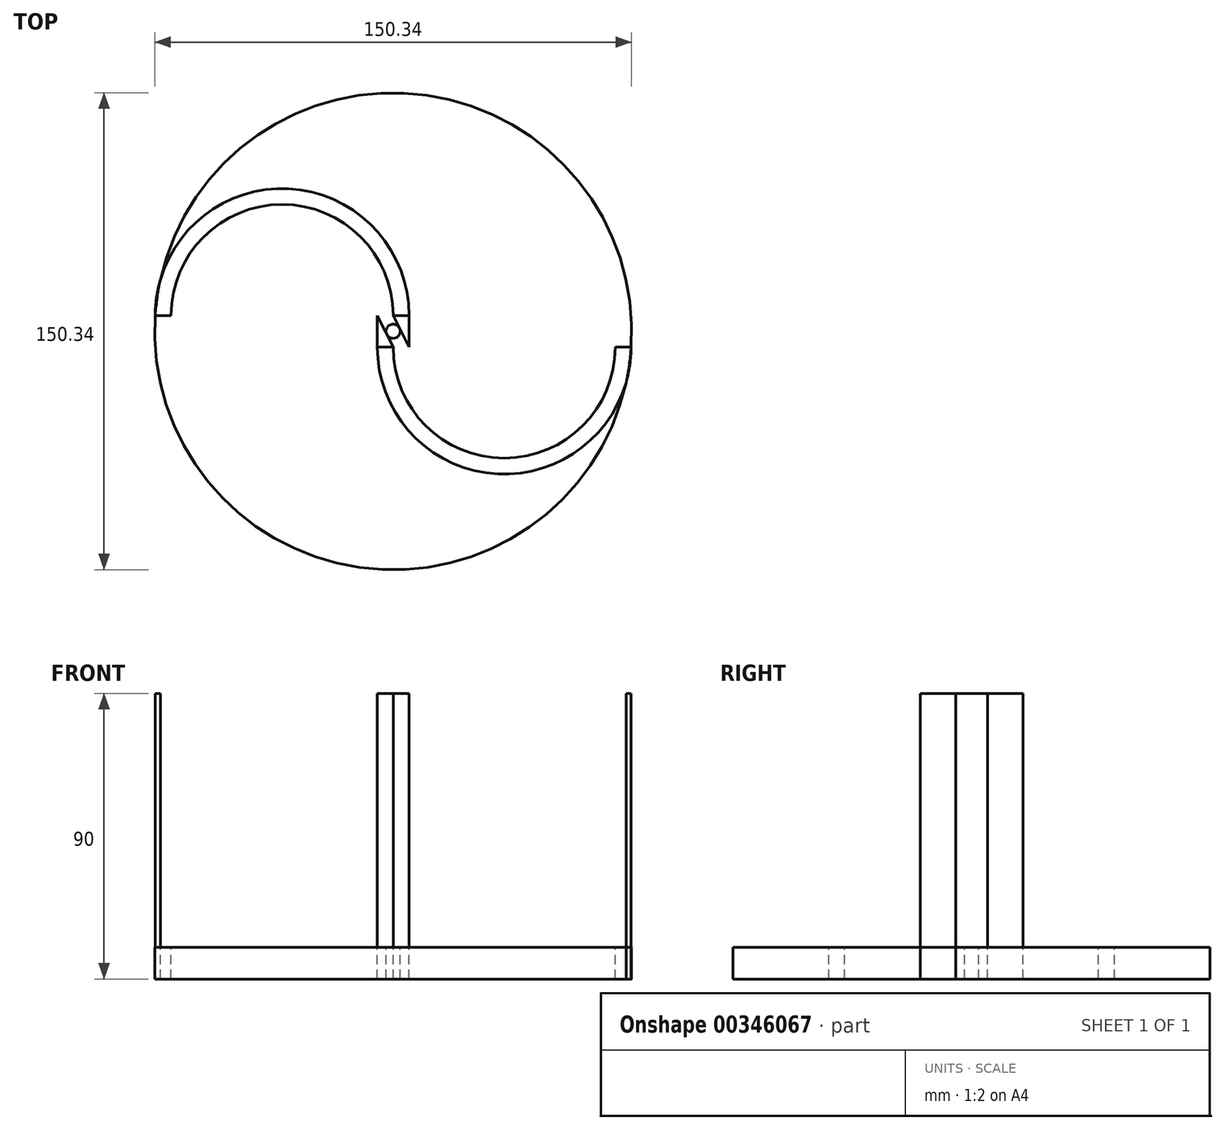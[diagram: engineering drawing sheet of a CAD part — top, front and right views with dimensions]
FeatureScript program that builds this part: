
annotation { "Feature Type Name" : "Feature", "Feature Type Description" : "" }
export const myFeature = defineFeature(function(context is Context, id is Id, definition is map)
    precondition{}
    {
        {
            var Q0;
            Q0=qCreatedBy(makeId("Top.planeOp"),FACE);
            var sketch = newSketch(context, id + "F0", { "sketchPlane" : qUnion([Q0])});
            skLineSegment(sketch, "E0.bottom", {"start": v(0, 0) * mm, "end": v(-10, 0) * mm});
            skLineSegment(sketch, "E0.top", {"start": v(0, 10) * mm, "end": v(-10, 10) * mm});
            skLineSegment(sketch, "E0.left", {"start": v(0, 0) * mm, "end": v(0, 10) * mm});
            skLineSegment(sketch, "E0.right", {"start": v(-10, 0) * mm, "end": v(-10, 10) * mm});
            skLineSegment(sketch, "E1", {"start": v(0, 10) * mm, "end": v(-80, 10) * mm});
            skArc(sketch, "E2", {"start": v(0, 10) * mm, "mid": v(-40, 50) * mm, "end": v(-80, 10) * mm});
            skLineSegment(sketch, "E3", {"start": v(-10, 0) * mm, "end": v(70, 0) * mm});
            skArc(sketch, "E4", {"start": v(-10, 0) * mm, "mid": v(30, -40) * mm, "end": v(70, 0) * mm});
            skLineSegment(sketch, "E5", {"start": v(0, 10) * mm, "end": v(-5, 10) * mm});
            skLineSegment(sketch, "E6", {"start": v(-80, 10) * mm, "end": v(-75, 10) * mm});
            skArc(sketch, "E7", {"start": v(-5, 10) * mm, "mid": v(-40, 45) * mm, "end": v(-75, 10) * mm});
            skLineSegment(sketch, "E8", {"start": v(-10, 0) * mm, "end": v(-5, 0) * mm});
            skLineSegment(sketch, "E9", {"start": v(70, 0) * mm, "end": v(65, 0) * mm});
            skArc(sketch, "E10", {"start": v(-5, 0) * mm, "mid": v(30, -35) * mm, "end": v(65, 0) * mm});
            skLineSegment(sketch, "E11", {"start": v(0, 0) * mm, "end": v(-5, 10) * mm});
            skLineSegment(sketch, "E12", {"start": v(-10, 10) * mm, "end": v(-5, 0) * mm});
            skCircle(sketch, "E13", {"center": v(-5, 5) * mm, "radius": 75.17 * mm});
            skPoint(sketch, "E13.centerSnap0", {"position": v(-10, 5) * mm});
            skCircle(sketch, "E14", {"center": v(-5, 5) * mm, "radius": 2.24 * mm});
            skSolve(sketch);
        }
        {
            var Q0;
            Q0=makeQuery(id+"F0.imprint","IMPRINT",FACE,{"disambiguationData":[TD([[makeQuery(id+"F0.imprint","IMPRINT",EDGE,{"derivedFrom":sQuery(id+"F0.wireOp",EDGE,"E4")}),1.0]])]});
            var Q1;
            Q1=makeQuery(id+"F0.imprint","IMPRINT",FACE,{"disambiguationData":[TD([[makeQuery(id+"F0.imprint","IMPRINT",EDGE,{"derivedFrom":sQuery(id+"F0.wireOp",EDGE,"E2")}),1.0]])]});
            var Q2;
            Q2=makeQuery(id+"F0.imprint","IMPRINT",FACE,{"disambiguationData":[TD([[makeQuery(id+"F0.imprint","IMPRINT",EDGE,{"derivedFrom":sQuery(id+"F0.wireOp",EDGE,"E0.left")}),1.0]])]});
            var Q3;
            Q3=makeQuery(id+"F0.imprint","IMPRINT",FACE,{"disambiguationData":[TD([[makeQuery(id+"F0.imprint","IMPRINT",EDGE,{"derivedFrom":sQuery(id+"F0.wireOp",EDGE,"E0.right")}),-1.0]])]});
            var Q4;
            {var subQ1=sQuery(id+"F0.wireOp",EDGE,"E5");Q4=makeQuery(id+"F0.imprint","IMPRINT",FACE,{"disambiguationData":[TD([[makeQuery(id+"F0.imprint","IMPRINT",EDGE,{"derivedFrom":subQ1}),-1.0]])]});}
            var Q5;
            {var subQ1=sQuery(id+"F0.wireOp",EDGE,"E8");Q5=makeQuery(id+"F0.imprint","IMPRINT",FACE,{"disambiguationData":[TD([[makeQuery(id+"F0.imprint","IMPRINT",EDGE,{"derivedFrom":subQ1}),-1.0]])]});}
            extrude(context, id + "F1", {"entities" : qUnion([Q0, Q1, Q2, Q3, Q4, Q5]), "depth" : 80 * mm});
        }
        {
            var Q0;
            {var subQ1=sQuery(id+"F0.wireOp",EDGE,"E0.right");Q0=makeQuery(id+"F0.imprint","IMPRINT",FACE,{"disambiguationData":[TD([[makeQuery(id+"F0.imprint","IMPRINT",EDGE,{"derivedFrom":subQ1}),1.0]])]});}
            var Q1;
            {var subQ1=sQuery(id+"F0.wireOp",EDGE,"E0.left");Q1=makeQuery(id+"F0.imprint","IMPRINT",FACE,{"disambiguationData":[TD([[makeQuery(id+"F0.imprint","IMPRINT",EDGE,{"derivedFrom":subQ1}),-1.0]])]});}
            var Q2;
            {var subQ2=sQuery(id+"F0.wireOp",EDGE,"E7");Q2=makeQuery(id+"F0.imprint","IMPRINT",FACE,{"disambiguationData":[TD([[makeQuery(id+"F0.imprint","IMPRINT",EDGE,{"derivedFrom":subQ2}),1.0]])]});}
            var Q3;
            {var subQ2=sQuery(id+"F0.wireOp",EDGE,"E10");Q3=makeQuery(id+"F0.imprint","IMPRINT",FACE,{"disambiguationData":[TD([[makeQuery(id+"F0.imprint","IMPRINT",EDGE,{"derivedFrom":subQ2}),1.0]])]});}
            var Q4;
            {var subQ1=sQuery(id+"F0.wireOp",EDGE,"E5");Q4=makeQuery(id+"F0.imprint","IMPRINT",FACE,{"disambiguationData":[TD([[makeQuery(id+"F0.imprint","IMPRINT",EDGE,{"derivedFrom":subQ1}),-1.0]])]});}
            var Q5;
            {var subQ1=sQuery(id+"F0.wireOp",EDGE,"E8");Q5=makeQuery(id+"F0.imprint","IMPRINT",FACE,{"disambiguationData":[TD([[makeQuery(id+"F0.imprint","IMPRINT",EDGE,{"derivedFrom":subQ1}),-1.0]])]});}
            var Q6;
            {var subQ0=sQuery(id+"F0.wireOp",EDGE,"E11");var subQ5=sQuery(id+"F0.wireOp",EDGE,"E14");var subQ6=makeQuery(id+"F0.imprint","INTERSECT",VERTEX,{"derivedFrom":[subQ0,subQ5]});Q6=makeQuery(id+"F0.imprint","IMPRINT",FACE,{"disambiguationData":[TD([[makeQuery(id+"F0.imprint","IMPRINT",EDGE,{"disambiguationData":[TD([[subQ6,1.0]])],"derivedFrom":subQ5}),-1.0]])]});}
            var Q7;
            {var subQ3=sQuery(id+"F0.wireOp",EDGE,"E11");var subQ5=sQuery(id+"F0.wireOp",EDGE,"E14");var subQ6=makeQuery(id+"F0.imprint","INTERSECT",VERTEX,{"derivedFrom":[subQ3,subQ5]});Q7=makeQuery(id+"F0.imprint","IMPRINT",FACE,{"disambiguationData":[TD([[makeQuery(id+"F0.imprint","IMPRINT",EDGE,{"disambiguationData":[TD([[subQ6,-1.0]])],"derivedFrom":subQ5}),-1.0]])]});}
            var Q8;
            {var subQ0=sQuery(id+"F0.wireOp",EDGE,"E0.right");Q8=makeQuery(id+"F0.imprint","IMPRINT",FACE,{"disambiguationData":[TD([[makeQuery(id+"F0.imprint","IMPRINT",EDGE,{"derivedFrom":subQ0}),-1.0]])]});}
            var Q9;
            {var subQ0=sQuery(id+"F0.wireOp",EDGE,"E0.left");Q9=makeQuery(id+"F0.imprint","IMPRINT",FACE,{"disambiguationData":[TD([[makeQuery(id+"F0.imprint","IMPRINT",EDGE,{"derivedFrom":subQ0}),1.0]])]});}
            extrude(context, id + "F2", {"entities" : qUnion([Q0, Q1, Q2, Q3, Q4, Q5, Q6, Q7, Q8, Q9]), "oppositeDirection" : true, "depth" : 10 * mm});
        }
    });
